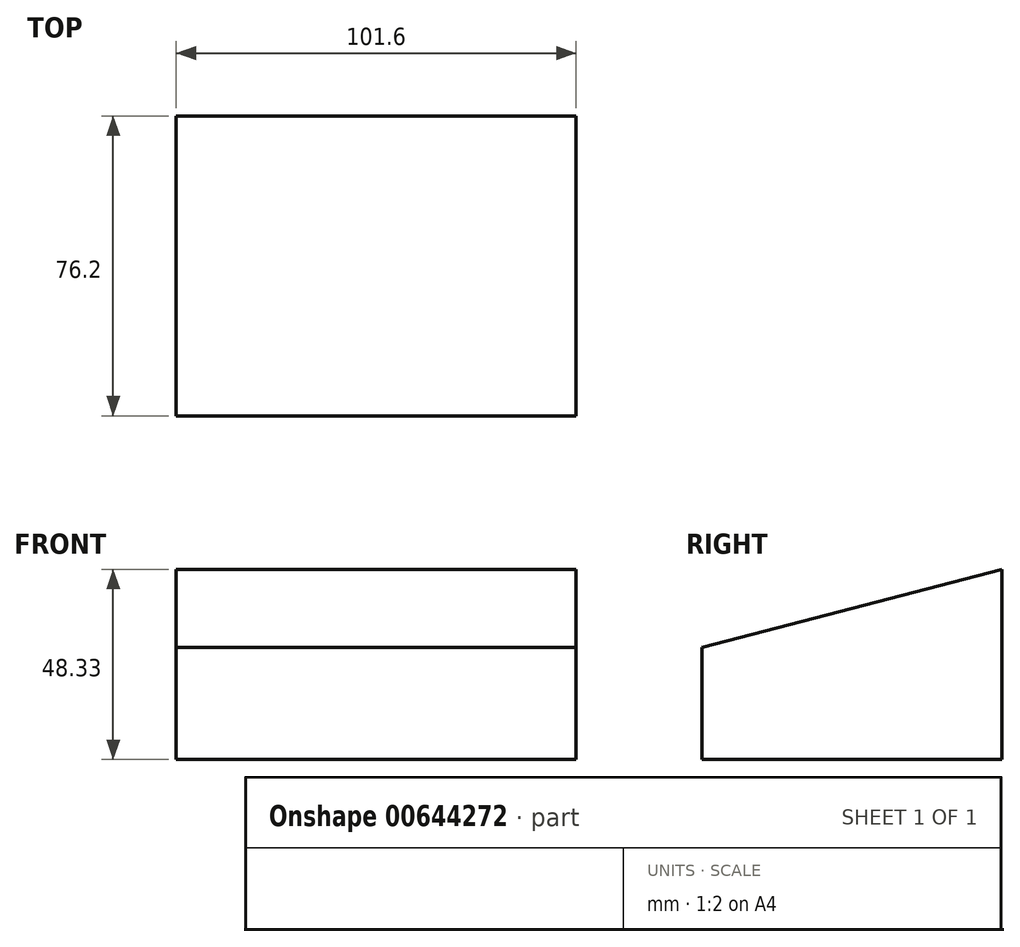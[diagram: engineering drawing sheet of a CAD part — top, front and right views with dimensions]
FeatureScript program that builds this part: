
annotation { "Feature Type Name" : "Feature", "Feature Type Description" : "" }
export const myFeature = defineFeature(function(context is Context, id is Id, definition is map)
    precondition{}
    {
        {
            var Q0;
            Q0=qCreatedBy(makeId("Top.planeOp"),FACE);
            var sketch = newSketch(context, id + "F0", { "sketchPlane" : qUnion([Q0])});
            skLineSegment(sketch, "E0.bottom", {"start": v(0, 0) * mm, "end": v(101.6, 0) * mm});
            skLineSegment(sketch, "E0.top", {"start": v(0, 76.2) * mm, "end": v(101.6, 76.2) * mm});
            skLineSegment(sketch, "E0.left", {"start": v(0, 0) * mm, "end": v(0, 76.2) * mm});
            skLineSegment(sketch, "E0.right", {"start": v(101.6, 0) * mm, "end": v(101.6, 76.2) * mm});
            skSolve(sketch);
        }
        {
            var Q0;
            Q0 = qSketchRegion(id + "F0", true);
            extrude(context, id + "F1", {"entities" : qUnion([Q0]), "depth" : 76.2 * mm, "offsetDistance" : 25.4 * mm});
        }
        {
            var Q0;
            Q0=makeQuery(id+"F1.opExtrude","SWEPT_FACE",FACE,{"disambiguationData":[OSD([sQuery(id+"F0.wireOp",EDGE,"E0.left")])]});
            var sketch = newSketch(context, id + "F2", { "sketchPlane" : qUnion([Q0])});
            skLineSegment(sketch, "E1", {"start": v(-76.2, 76.2) * mm, "end": v(0, 28.47) * mm});
            skLineSegment(sketch, "E2", {"start": v(0, 28.47) * mm, "end": v(-76.2, 48.33) * mm});
            skLineSegment(sketch, "E3", {"start": v(-76.2, 48.33) * mm, "end": v(-76.2, 76.2) * mm});
            skLineSegment(sketch, "E4", {"start": v(0, 76.2) * mm, "end": v(-76.2, 76.2) * mm});
            skLineSegment(sketch, "E5", {"start": v(0, 76.2) * mm, "end": v(0, 28.47) * mm});
            skSolve(sketch);
        }
        {
            var Q0;
            Q0=makeQuery(id+"F2.imprint","IMPRINT",FACE,{"disambiguationData":[TD([[makeQuery(id+"F2.imprint","IMPRINT",EDGE,{"derivedFrom":sQuery(id+"F2.wireOp",EDGE,"E1")}),1.0]])]});
            var Q1;
            Q1=makeQuery(id+"F2.imprint","IMPRINT",FACE,{"disambiguationData":[TD([[makeQuery(id+"F2.imprint","IMPRINT",EDGE,{"derivedFrom":sQuery(id+"F2.wireOp",EDGE,"E1")}),-1.0]])]});
            extrude(context, id + "F3", {"entities" : qUnion([Q0, Q1]), "operationType" : NewBodyOperationType.REMOVE, "oppositeDirection" : true, "depth" : 127 * mm, "offsetDistance" : 25.4 * mm});
        }
    });
